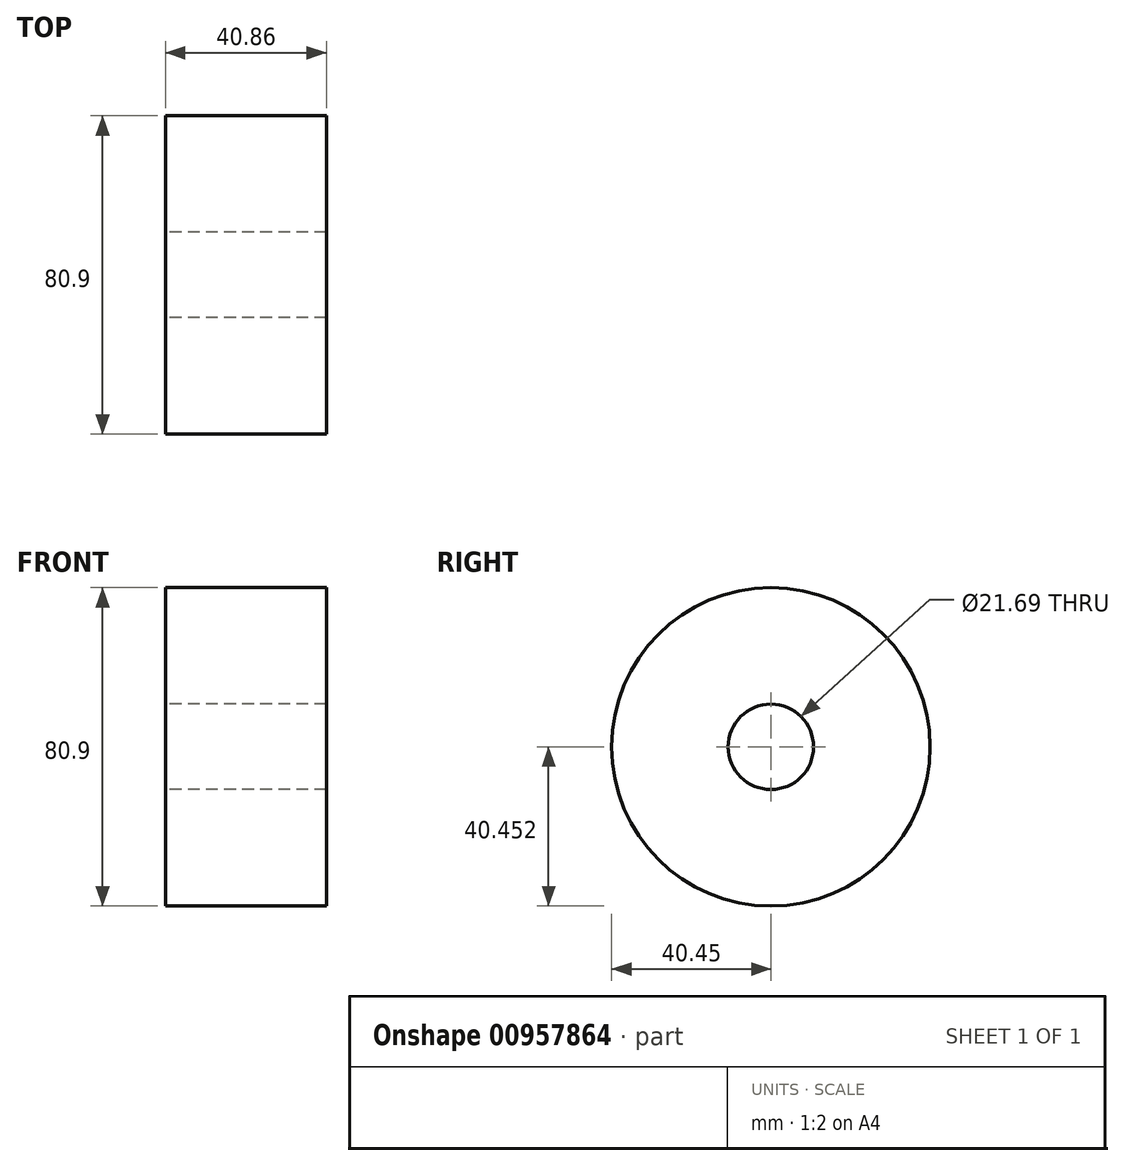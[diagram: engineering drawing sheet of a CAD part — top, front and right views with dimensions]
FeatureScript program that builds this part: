
annotation { "Feature Type Name" : "Feature", "Feature Type Description" : "" }
export const myFeature = defineFeature(function(context is Context, id is Id, definition is map)
    precondition{}
    {
        {
            var Q0;
            Q0=qCreatedBy(makeId("Front.planeOp"),FACE);
            var sketch = newSketch(context, id + "F0", { "sketchPlane" : qUnion([Q0])});
            skLineSegment(sketch, "E0.bottom", {"start": v(20.43, -14.8) * mm, "end": v(-20.43, -14.8) * mm});
            skLineSegment(sketch, "E0.top", {"start": v(20.43, 14.8) * mm, "end": v(-20.43, 14.8) * mm});
            skLineSegment(sketch, "E0.left", {"start": v(20.43, -14.8) * mm, "end": v(20.43, 14.8) * mm});
            skLineSegment(sketch, "E0.right", {"start": v(-20.43, -14.8) * mm, "end": v(-20.43, 14.8) * mm});
            skPoint(sketch, "E0.middle", {"position": v(0, 0) * mm});
            skLineSegment(sketch, "E1", {"start": v(-28.54, -25.65) * mm, "end": v(38.65, -25.65) * mm, "construction": true});
            skSolve(sketch);
        }
        {
            var Q0;
            Q0=makeQuery(id+"F0.imprint","IMPRINT",FACE,{"disambiguationData":[TD([[makeQuery(id+"F0.imprint","IMPRINT",EDGE,{"derivedFrom":sQuery(id+"F0.wireOp",EDGE,"E0.bottom")}),-1.0]])]});
            var Q1;
            Q1=sQuery(id+"F0.wireOp",EDGE,"E1");
            revolve(context, id + "F1", {"surfaceOperationType" : NewSurfaceOperationType.NEW, "entities" : qUnion([Q0]), "axis" : qUnion([Q1]), "revolveType" : RevolveType.FULL});
        }
    });
